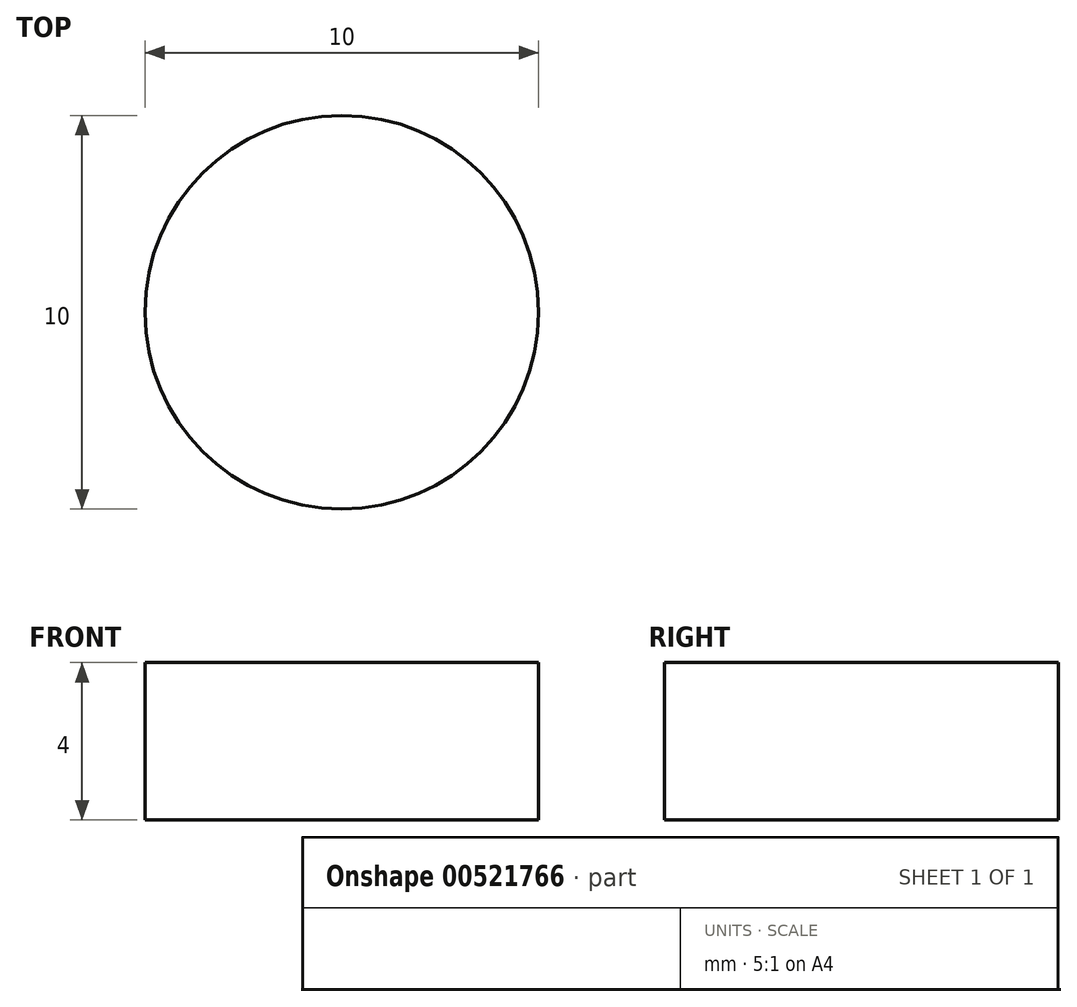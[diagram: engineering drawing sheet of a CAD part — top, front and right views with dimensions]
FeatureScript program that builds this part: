
annotation { "Feature Type Name" : "Feature", "Feature Type Description" : "" }
export const myFeature = defineFeature(function(context is Context, id is Id, definition is map)
    precondition{}
    {
        {
            var Q0;
            Q0=qCreatedBy(makeId("Top.planeOp"),FACE);
            var sketch = newSketch(context, id + "F0", { "sketchPlane" : qUnion([Q0])});
            skCircle(sketch, "E0", {"center": v(0, 0) * mm, "radius": 5 * mm});
            skSolve(sketch);
        }
        {
            var Q0;
            Q0=makeQuery(id+"F0.imprint","IMPRINT",FACE,{"disambiguationData":[TD([[makeQuery(id+"F0.imprint","IMPRINT",EDGE,{"derivedFrom":sQuery(id+"F0.wireOp",EDGE,"E0")}),1.0]])]});
            extrude(context, id + "F1", {"entities" : qUnion([Q0]), "depth" : 4 * mm, "offsetDistance" : 25 * mm});
        }
    });
